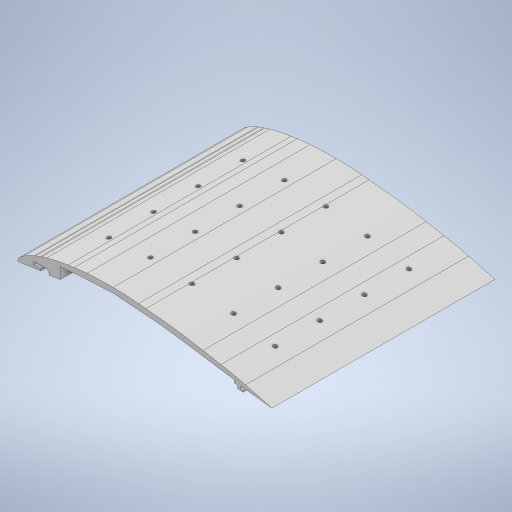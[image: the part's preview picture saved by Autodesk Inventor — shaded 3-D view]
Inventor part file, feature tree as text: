
AUTODESK INVENTOR PART (.ipt)
format: ipt  version: 2024.1 (Build 281209000, 209)  size: 512,512 bytes
history: native  units: in
note: dims shown in document units (in); Inventor stores cm internally (conversion verified against a paired STEP export)
features: sketch x11, extrude x9, other x3, plane x1
ambient origin geometry x8: Origin, YZ Plane, XZ Plane, XY Plane, X Axis, Y Axis, Z Axis, Center Point
bodies: Solid1 (feature_tree)
feature tree (24):
  other  "Airfoil.ipt"
  extrude  "Extrusion1"  Depth=0.3937in
  plane  "Work Plane1"
  extrude  "Extrusion2"  [1 undecoded]
  extrude  "Extrusion3"  Depth=8.4646in TaperAngle=0.0deg
  extrude  "Extrusion4"  Depth=0.1575in
  extrude  "Extrusion5"  Depth=0.1575in
  extrude  "Extrusion6"  Depth=0.1575in
  extrude  "Extrusion7"  Depth=0.1575in
  extrude  "Extrusion8"  Depth=0.1575in
  extrude  "Extrusion9"  Depth=0.1575in
  sketch  "Sketch15"  dims[d33=0.1575in]
  sketch  "Sketch16"  dims[d34=0.1575in d35=0.1575in d36=0.1575in d37=0.1575in d38=0.1575in d39=0.1575in d40=0.1575in d41=0.1575in d42=1.9685in d43=0.0in d44=8.4646in d45=0.0in d46=8.4646in d47=0.0in d48=8.4646in d49=0.0in d50=8.4646in d51=0.0in d52=8.4646in d53=0.0in d54=1.771in]
  other  "Solid1::Airfoil.ipt"
  other  "TaggingFeature1"
  sketch  "Sketch4"  dims[d0=0.3937in d3=0.1969in]
  sketch  "Sketch5"  dims[d4=8.4646in d5=0.0in d6=-8.4646in]
  sketch  "Sketch7"  dims[d7=39.3701in d8=0.0in d10=8.4646in d11=0.0in]
  sketch  "Sketch8"  dims[d12=1.6929in d21=0.1575in]
  sketch  "Sketch10"  dims[d22=0.1575in d23=0.1575in]
  sketch  "Sketch11"  dims[d24=0.1575in d25=0.1575in]
  sketch  "Sketch12"  dims[d27=0.1575in d28=0.1575in]
  sketch  "Sketch13"  dims[d29=0.1575in d30=0.1575in]
  sketch  "Sketch14"  dims[d31=0.1575in d32=0.1575in]
note: 1 required parameter value undecoded (feature->parameter linkage not recoverable at this tier; creation-order binding heuristic only, values carry confidence <= 0.55)
